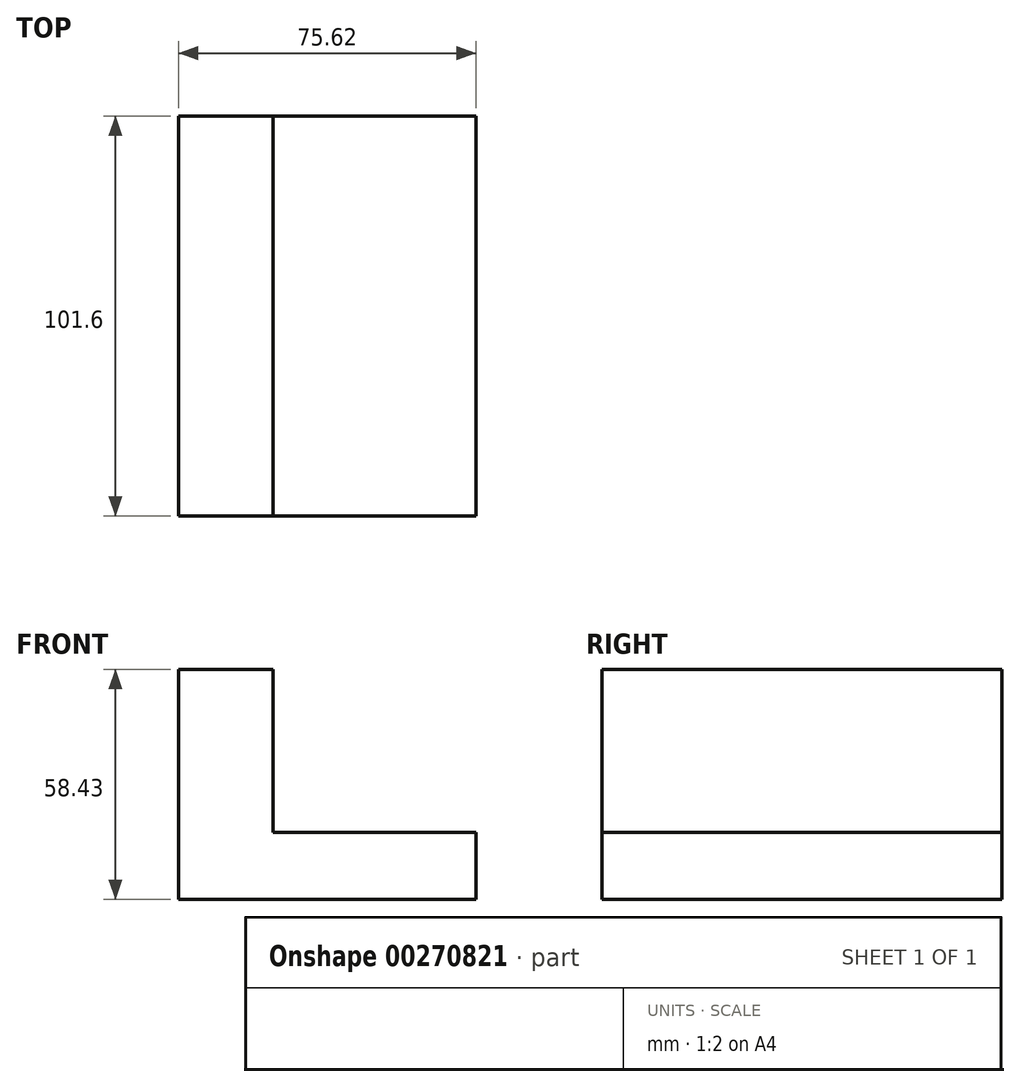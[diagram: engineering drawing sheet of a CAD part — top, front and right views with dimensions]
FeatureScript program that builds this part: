
annotation { "Feature Type Name" : "Feature", "Feature Type Description" : "" }
export const myFeature = defineFeature(function(context is Context, id is Id, definition is map)
    precondition{}
    {
        {
            var Q0;
            Q0=qCreatedBy(makeId("Front.planeOp"),FACE);
            var sketch = newSketch(context, id + "F0", { "sketchPlane" : qUnion([Q0])});
            skLineSegment(sketch, "E0", {"start": v(0, 0) * mm, "end": v(-75.62, 0) * mm});
            skLineSegment(sketch, "E1", {"start": v(-75.62, 0) * mm, "end": v(-75.62, 58.43) * mm});
            skLineSegment(sketch, "E2", {"start": v(-75.62, 58.43) * mm, "end": v(-51.56, 58.43) * mm});
            skLineSegment(sketch, "E3", {"start": v(-51.56, 58.43) * mm, "end": v(-51.56, 17) * mm});
            skLineSegment(sketch, "E4", {"start": v(-51.56, 17) * mm, "end": v(0, 17) * mm});
            skLineSegment(sketch, "E5", {"start": v(0, 17) * mm, "end": v(0, 0) * mm});
            skSolve(sketch);
        }
        {
            var Q0;
            Q0 = qSketchRegion(id + "F0", true);
            extrude(context, id + "F1", {"entities" : qUnion([Q0]), "depth" : 101.6 * mm});
        }
    });
